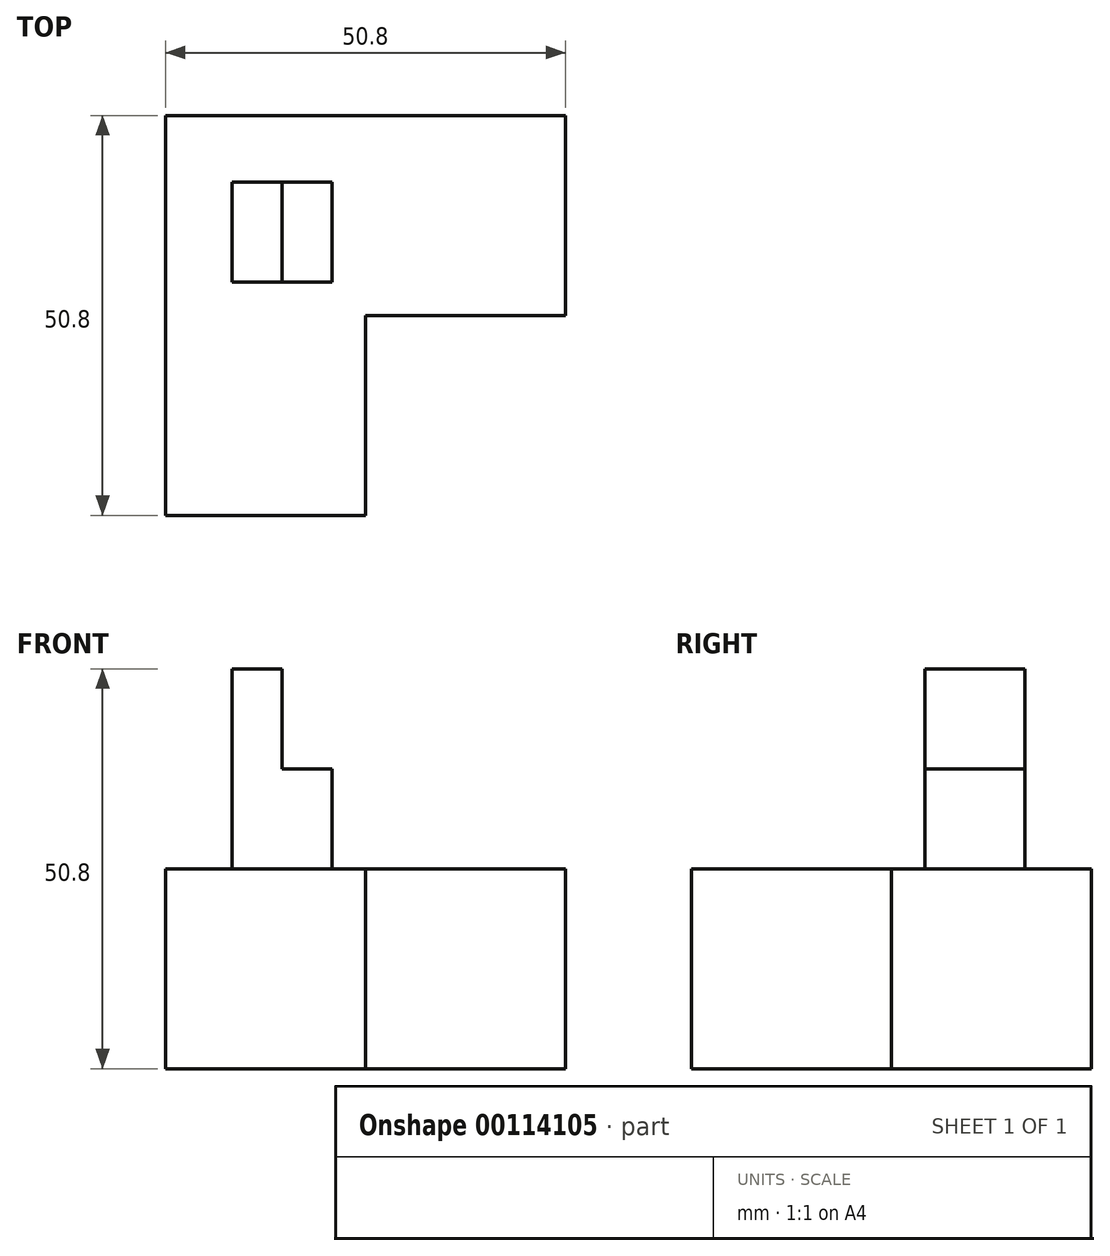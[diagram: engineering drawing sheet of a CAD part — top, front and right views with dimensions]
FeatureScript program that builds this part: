
annotation { "Feature Type Name" : "Feature", "Feature Type Description" : "" }
export const myFeature = defineFeature(function(context is Context, id is Id, definition is map)
    precondition{}
    {
        {
            var Q0;
            Q0=qCreatedBy(makeId("Top.planeOp"),FACE);
            var sketch = newSketch(context, id + "F0", { "sketchPlane" : qUnion([Q0])});
            skLineSegment(sketch, "E0.bottom", {"start": v(25.4, 12.7) * mm, "end": v(-25.4, 12.7) * mm});
            skLineSegment(sketch, "E0.top", {"start": v(25.4, -12.7) * mm, "end": v(0, -12.7) * mm});
            skLineSegment(sketch, "E0.left", {"start": v(25.4, 12.7) * mm, "end": v(25.4, -12.7) * mm});
            skLineSegment(sketch, "E0.right", {"start": v(-25.4, 12.7) * mm, "end": v(-25.4, -12.7) * mm});
            skPoint(sketch, "E0.middle", {"position": v(0, 0) * mm});
            skLineSegment(sketch, "E1.bottom", {"start": v(-25.4, 12.7) * mm, "end": v(0, 12.7) * mm});
            skLineSegment(sketch, "E1.top", {"start": v(-25.4, -38.1) * mm, "end": v(0, -38.1) * mm});
            skLineSegment(sketch, "E1.left", {"start": v(-25.4, 12.7) * mm, "end": v(-25.4, -38.1) * mm});
            skLineSegment(sketch, "E2.trimOffspring", {"start": v(0, -12.7) * mm, "end": v(0, -38.1) * mm});
            skSolve(sketch);
        }
        {
            var Q0;
            Q0 = qSketchRegion(id + "F0", true);
            extrude(context, id + "F1", {"entities" : qUnion([Q0]), "depth" : 25.4 * mm});
        }
        {
            var Q0;
            Q0=makeQuery(id+"F1.opExtrude","CAP_FACE",FACE,{"disambiguationData":[OSD([sQuery(id+"F0.wireOp",EDGE,"E0.bottom"),sQuery(id+"F0.wireOp",EDGE,"E0.top"),sQuery(id+"F0.wireOp",EDGE,"E0.left"),sQuery(id+"F0.wireOp",EDGE,"E1.bottom"),sQuery(id+"F0.wireOp",EDGE,"E1.top"),sQuery(id+"F0.wireOp",EDGE,"E1.left"),sQuery(id+"F0.wireOp",EDGE,"E2.trimOffspring")])],"isStart":false});
            var sketch = newSketch(context, id + "F2", { "sketchPlane" : qUnion([Q0])});
            skLineSegment(sketch, "E3.0", {"start": v(-16.94, -8.46) * mm, "end": v(-16.94, 4.24) * mm});
            skLineSegment(sketch, "E3.1", {"start": v(-4.24, -8.46) * mm, "end": v(-16.94, -8.46) * mm});
            skLineSegment(sketch, "E3.2", {"start": v(-4.24, -8.46) * mm, "end": v(-4.24, 4.24) * mm});
            skLineSegment(sketch, "E3.3", {"start": v(-4.24, 4.24) * mm, "end": v(-16.94, 4.24) * mm});
            skSolve(sketch);
        }
        {
            var Q0;
            Q0 = qSketchRegion(id + "F2", true);
            extrude(context, id + "F3", {"entities" : qUnion([Q0]), "operationType" : NewBodyOperationType.ADD, "depth" : 25.4 * mm});
        }
        {
            var Q0;
            Q0=makeQuery(id+"F3.opExtrude","CAP_FACE",FACE,{"disambiguationData":[OSD([sQuery(id+"F2.wireOp",EDGE,"E3.0"),sQuery(id+"F2.wireOp",EDGE,"E3.1"),sQuery(id+"F2.wireOp",EDGE,"E3.2"),sQuery(id+"F2.wireOp",EDGE,"E3.3")])],"isStart":false});
            var sketch = newSketch(context, id + "F4", { "sketchPlane" : qUnion([Q0])});
            skLineSegment(sketch, "E4.bottom", {"start": v(-4.24, 4.24) * mm, "end": v(-10.6, 4.24) * mm});
            skLineSegment(sketch, "E4.top", {"start": v(-4.24, -8.46) * mm, "end": v(-10.6, -8.46) * mm});
            skLineSegment(sketch, "E4.left", {"start": v(-4.24, 4.24) * mm, "end": v(-4.24, -8.46) * mm});
            skLineSegment(sketch, "E4.right", {"start": v(-10.6, 4.24) * mm, "end": v(-10.6, -8.46) * mm});
            skSolve(sketch);
        }
        {
            var Q0;
            Q0 = qSketchRegion(id + "F4", true);
            extrude(context, id + "F5", {"entities" : qUnion([Q0]), "operationType" : NewBodyOperationType.REMOVE, "oppositeDirection" : true, "depth" : 12.7 * mm});
        }
    });
